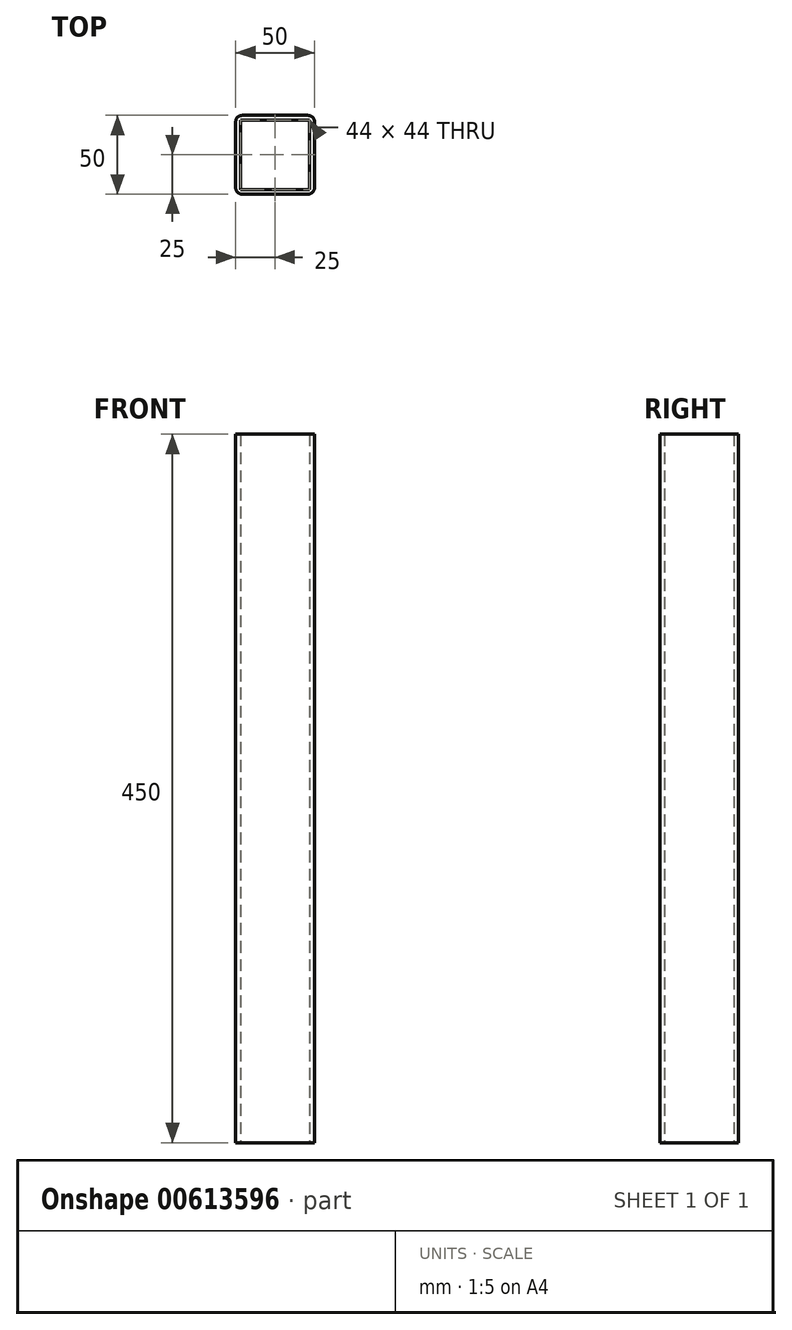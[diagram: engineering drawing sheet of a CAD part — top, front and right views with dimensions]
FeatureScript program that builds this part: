
annotation { "Feature Type Name" : "Feature", "Feature Type Description" : "" }
export const myFeature = defineFeature(function(context is Context, id is Id, definition is map)
    precondition{}
    {
        {
            var Q0;
            Q0=qCreatedBy(makeId("Top.planeOp"),FACE);
            var sketch = newSketch(context, id + "F0", { "sketchPlane" : qUnion([Q0])});
            skLineSegment(sketch, "E0.bottom", {"start": v(4, 0) * mm, "end": v(46, 0) * mm});
            skLineSegment(sketch, "E0.top", {"start": v(4, 50) * mm, "end": v(46, 50) * mm});
            skLineSegment(sketch, "E0.left", {"start": v(0, 4) * mm, "end": v(0, 46) * mm});
            skLineSegment(sketch, "E0.right", {"start": v(50, 4) * mm, "end": v(50, 46) * mm});
            skPoint(sketch, "E1.visualSharp", {"position": v(50, 0) * mm});
            skArc(sketch, "E1.filletArc", {"start": v(46, 0) * mm, "mid": v(48.83, 1.17) * mm, "end": v(50, 4) * mm});
            skPoint(sketch, "E2.visualSharp", {"position": v(50, 50) * mm});
            skArc(sketch, "E2.filletArc", {"start": v(50, 46) * mm, "mid": v(48.83, 48.83) * mm, "end": v(46, 50) * mm});
            skPoint(sketch, "E3.visualSharp", {"position": v(0, 50) * mm});
            skArc(sketch, "E3.filletArc", {"start": v(4, 50) * mm, "mid": v(1.17, 48.83) * mm, "end": v(0, 46) * mm});
            skPoint(sketch, "E4.visualSharp", {"position": v(0, 0) * mm});
            skArc(sketch, "E4.filletArc", {"start": v(0, 4) * mm, "mid": v(1.17, 1.17) * mm, "end": v(4, 0) * mm});
            skLineSegment(sketch, "E5.0", {"start": v(3, 47) * mm, "end": v(47, 47) * mm});
            skLineSegment(sketch, "E5.1", {"start": v(3, 3) * mm, "end": v(3, 47) * mm});
            skLineSegment(sketch, "E5.2", {"start": v(3, 3) * mm, "end": v(47, 3) * mm});
            skLineSegment(sketch, "E5.3", {"start": v(47, 3) * mm, "end": v(47, 47) * mm});
            skSolve(sketch);
        }
        {
            var Q0;
            Q0=qSketchRegion(id+"F0",true);
            extrude(context, id + "F1", {"entities" : qUnion([Q0]), "depth" : 450 * mm, "offsetDistance" : 25 * mm});
        }
    });
